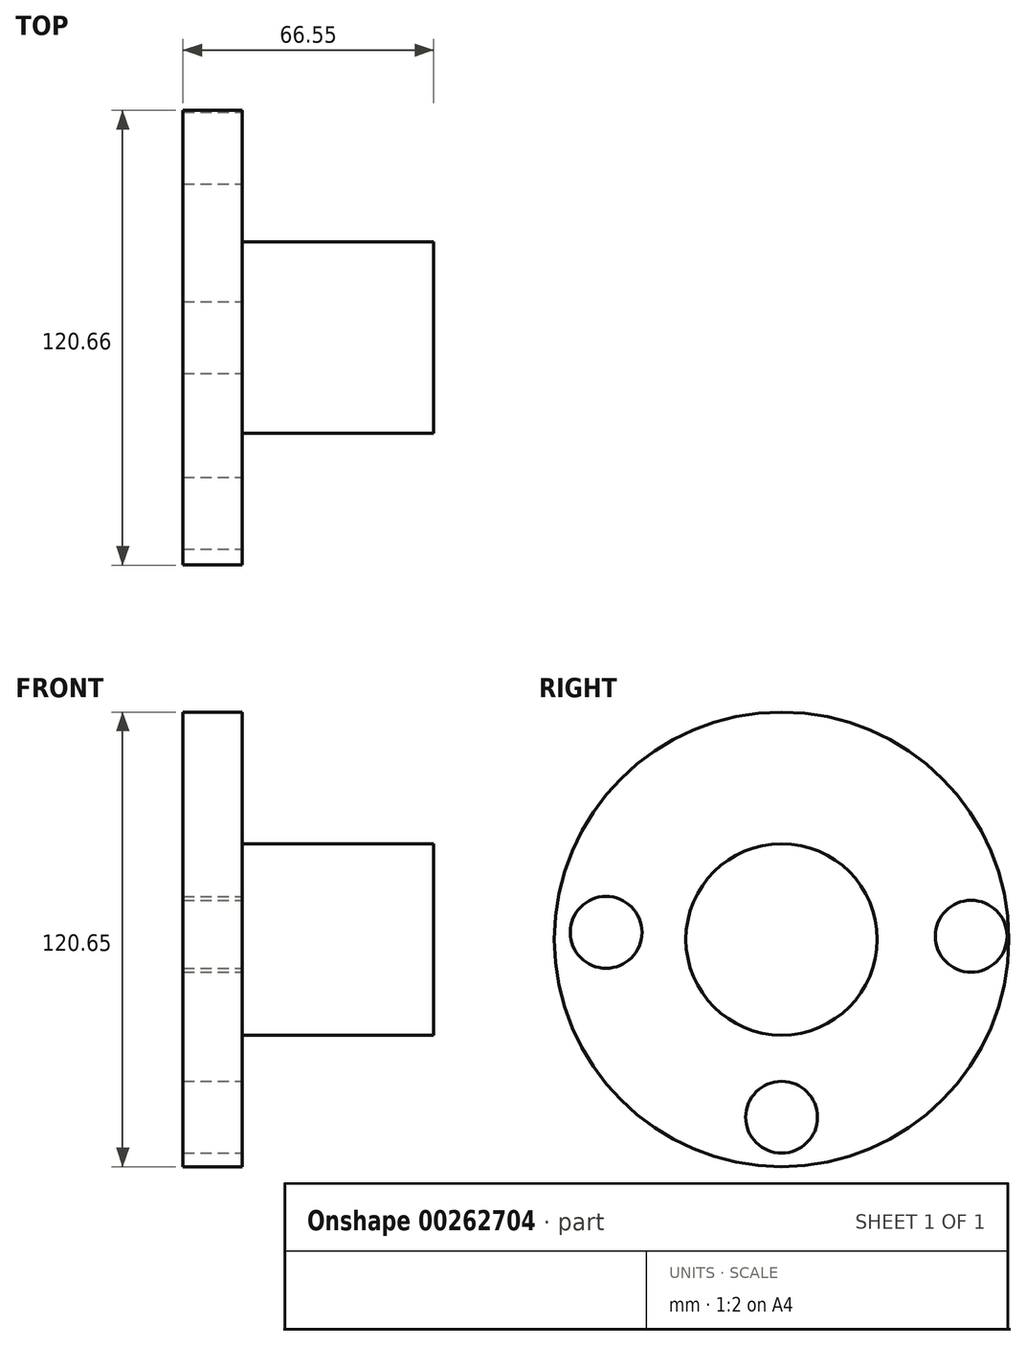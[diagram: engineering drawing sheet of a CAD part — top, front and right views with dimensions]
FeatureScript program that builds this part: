
annotation { "Feature Type Name" : "Feature", "Feature Type Description" : "" }
export const myFeature = defineFeature(function(context is Context, id is Id, definition is map)
    precondition{}
    {
        {
            var Q0;
            Q0=qCreatedBy(makeId("Front.planeOp"),FACE);
            var sketch = newSketch(context, id + "F0", { "sketchPlane" : qUnion([Q0])});
            skLineSegment(sketch, "E0", {"start": v(-60.75, 53.03) * mm, "end": v(-60.75, -7.3) * mm});
            skLineSegment(sketch, "E1", {"start": v(-60.75, -7.3) * mm, "end": v(5.8, -7.3) * mm});
            skLineSegment(sketch, "E2", {"start": v(5.8, -7.3) * mm, "end": v(5.8, 18.1) * mm});
            skLineSegment(sketch, "E3", {"start": v(5.8, 18.1) * mm, "end": v(-45, 18.1) * mm});
            skLineSegment(sketch, "E4", {"start": v(-45, 18.1) * mm, "end": v(-45, 53.03) * mm});
            skLineSegment(sketch, "E5", {"start": v(-45, 53.03) * mm, "end": v(-60.75, 53.03) * mm});
            skSolve(sketch);
        }
        {
            var Q0;
            Q0=makeQuery(id+"F0.imprint","IMPRINT",FACE,{"disambiguationData":[TD([[makeQuery(id+"F0.imprint","IMPRINT",EDGE,{"derivedFrom":sQuery(id+"F0.wireOp",EDGE,"E0")}),1.0]])]});
            var Q1;
            Q1=sQuery(id+"F0.wireOp",EDGE,"E1");
            revolve(context, id + "F1", {"entities" : qUnion([Q0]), "axis" : qUnion([Q1]), "revolveType" : RevolveType.FULL});
        }
        {
            var Q0;
            Q0=makeQuery(id+"F1.opRevolve","SWEPT_FACE",FACE,{"disambiguationData":[OSD([sQuery(id+"F0.wireOp",EDGE,"E4")])]});
            var sketch = newSketch(context, id + "F2", { "sketchPlane" : qUnion([Q0])});
            skCircle(sketch, "E6", {"center": v(50.3, -6.47) * mm, "radius": 9.52 * mm});
            skSolve(sketch);
        }
        {
            var Q0;
            Q0 = qSketchRegion(id + "F2", true);
            extrude(context, id + "F3", {"entities" : qUnion([Q0]), "operationType" : NewBodyOperationType.REMOVE, "oppositeDirection" : true, "depth" : 508.5 * mm});
        }
        {
            var Q0;
            Q0=makeQuery(id+"F1.opRevolve","SWEPT_FACE",FACE,{"disambiguationData":[OSD([sQuery(id+"F0.wireOp",EDGE,"E4")])]});
            var sketch = newSketch(context, id + "F4", { "sketchPlane" : qUnion([Q0])});
            skCircle(sketch, "E7", {"center": v(-46.6, -5.43) * mm, "radius": 9.53 * mm});
            skSolve(sketch);
        }
        {
            var Q0;
            Q0 = qSketchRegion(id + "F4", true);
            extrude(context, id + "F5", {"entities" : qUnion([Q0]), "operationType" : NewBodyOperationType.REMOVE, "oppositeDirection" : true, "depth" : 25.4 * mm});
        }
        {
            var Q0;
            Q0=makeQuery(id+"F1.opRevolve","SWEPT_FACE",FACE,{"disambiguationData":[OSD([sQuery(id+"F0.wireOp",EDGE,"E4")])]});
            var sketch = newSketch(context, id + "F6", { "sketchPlane" : qUnion([Q0])});
            skCircle(sketch, "E8", {"center": v(0, -54.5) * mm, "radius": 9.53 * mm});
            skSolve(sketch);
        }
        {
            var Q0;
            Q0 = qSketchRegion(id + "F6", true);
            extrude(context, id + "F7", {"entities" : qUnion([Q0]), "operationType" : NewBodyOperationType.REMOVE, "oppositeDirection" : true, "depth" : 25.4 * mm});
        }
    });
